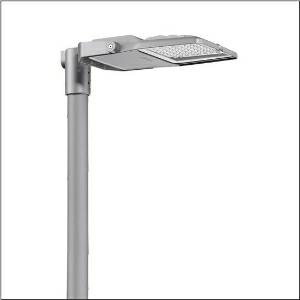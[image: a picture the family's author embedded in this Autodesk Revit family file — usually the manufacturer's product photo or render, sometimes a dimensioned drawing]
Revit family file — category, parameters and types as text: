
# Revit family: floodlight_fl_21_iq_mini___pl43_5xa7771b4a3a_ae81
name_source: partatom
category: Lighting Fixtures
units: mm (PartAtom-declared; Revit-internal decimal feet)

## family parameters
Cut with Voids When Loaded = No
Host = Face
Light Source = No
Part Type = Normal
Room Calculation Point = No
Round Connector Dimension = Use Diameter
Shared = No

## types (1)
- --- (1 x LED, 6660 lm, 45.5 W, 4000K)
    Apparent Load = 46 VA
    CIE Flux Codes = 27 78 99 100 100
    Color Rendering = 70
    Color Temperature = 4000K
    Default Elevation = 1800 mm
    Description = Floodlight FL 21 iQ mini, floodlight, primary light control with lens, of PMMA, primary optical cover: protective disc, of toughened safety glass, transparent, light distribution: PL43, light emission: direct distribution, installation type: surface-mounted, lamps: LED, High Power LED, rated values: 6.660lm | 45,5W | 146,4lm/W (begin service life); end service life: 6.660lm | 48W; at 50% lumin. flux: 3.330lm | 21,5W | 154,9lm/W, colour temperature: 4000K, colour rendering: CRI > 70, light colour: 740, light setting 1 begin service life: 100% | 6.660lm | 45,5W | 146,4lm/W | 4.000K, light setting 1 end service life: 48W, further light settings possible, control: Auto-Match, Temp-Guard, Lumen-Switch, Night-Set, Smart-Wire, Light-Fading, Desk-Remote (wireless, voltage-free reading and setting of iQ features in the workshop via application-optimized NFC function/RFID function), optimised constant luminous flux control (CLO 2.0), pre-setting: linear dimming characteristic, with terminal, 6-pole, mains connection: 220..240V, AC, 50/60Hz, luminaire housing, of diecast aluminium, powder-coated, SITECO metallic grey (DB 702S), corrosivity category C5 mid according to DIN EN ISO 12944suitable for swimming poolschlorine-resistant, sealing non-destructively replaceable, please order mast flange separately, mast bracket, of steel, galvanised, powder-coated, SITECO metallic grey (DB 702S), protection rating (complete): IP66, insulation class (complete): insulation class II (safety insulation), certification: CE, ENEC, VDE, protection symbol: D, impact resistance: IK08, permissible operating ambient temperature: -40..+40°C, permissible operating ambient temperature for outdoor applications: -40..+50°C, standard: DIN EN 12944, LABS conformity tested according to VDMA 24364:2018-05, packaging unit: 1 piece

Light Distribution: PL43
    Height = 70 mm
    Lamp = 1 x LED
    Lamp Light Flux = 6660 lm
    Lamp Power = 45.5 W
    Lamp count = 1
    Length = 485 mm
    Luminous efficacy = 146 lm/W
    Manufacturer = Siteco
    ModVariant = No
    Model = 5XA7771B4A3A
    Number of Poles = 1
    OnlyDefault = Yes
    Power Factor = 1
    Product Name = Floodlight FL 21 iQ mini | PL43
    Product group = floodlight | pylon annexe
    ProductGroupID = 6201
    Protection Class = Protection class II
    Protection Degree = IP 66
    RLX_Detail_Level = 1
    RLX_Emergency_Light_Flux = 0 lm
    RLX_Emergency_Type = 0
    RLX_Emergency_Type_DB = No
    RlxData = <blob elided: 101289 chars, md5=045423ed>
    Socket = socket
    Standby Power = 0 W
    System Light Flux = 6660 lm
    System Power = 46 W
    Type Comments = factory setting: luminous flux: 100 % | dim-lin: 254 | 463 mA
    Type Image = l_1007125.jpg
    URL = http://relux.com
    VarID = @adj_162359
    Voltage = 0 V
    Weight = 0.00 kg
    Width = 337 mm

## geometry (parser evidence)
native form markers: Blend x4, Sweep x12
no freeform markers — native parametric forms only
